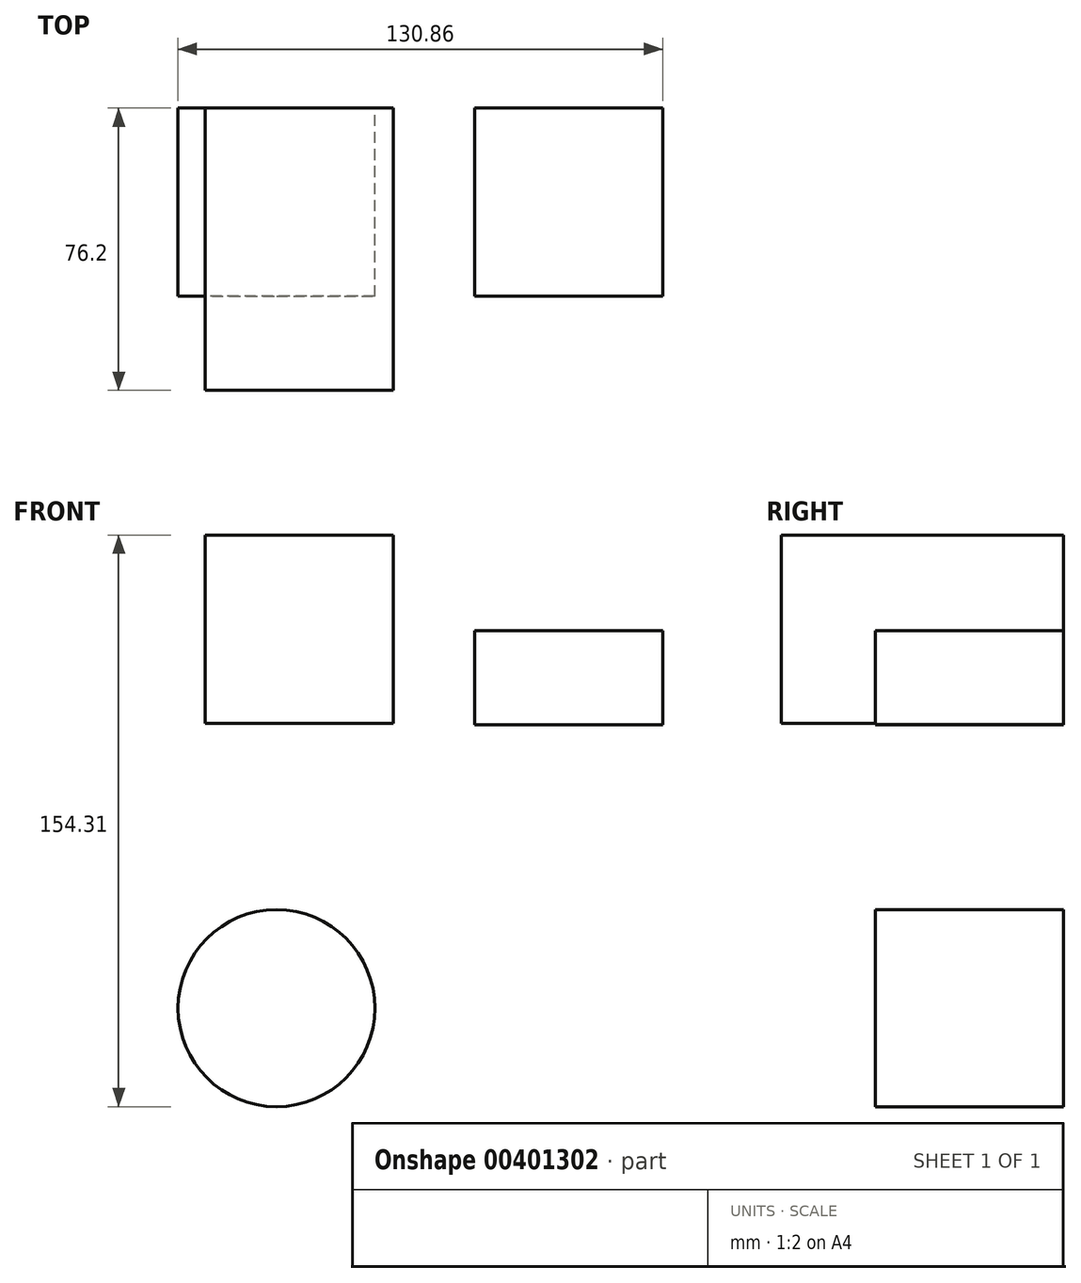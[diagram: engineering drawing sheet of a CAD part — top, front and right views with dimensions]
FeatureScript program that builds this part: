
annotation { "Feature Type Name" : "Feature", "Feature Type Description" : "" }
export const myFeature = defineFeature(function(context is Context, id is Id, definition is map)
    precondition{}
    {
        {
            var Q0;
            Q0=qCreatedBy(makeId("Front.planeOp"),FACE);
            var sketch = newSketch(context, id + "F0", { "sketchPlane" : qUnion([Q0])});
            skLineSegment(sketch, "E0.bottom", {"start": v(-61.9, 87.41) * mm, "end": v(-11.1, 87.41) * mm});
            skLineSegment(sketch, "E0.top", {"start": v(-61.9, 36.61) * mm, "end": v(-11.1, 36.61) * mm});
            skLineSegment(sketch, "E0.left", {"start": v(-61.9, 87.41) * mm, "end": v(-61.9, 36.61) * mm});
            skLineSegment(sketch, "E0.right", {"start": v(-11.1, 87.41) * mm, "end": v(-11.1, 36.61) * mm});
            skSolve(sketch);
        }
        {
            var Q0;
            Q0=qCreatedBy(makeId("Front.planeOp"),FACE);
            var sketch = newSketch(context, id + "F1", { "sketchPlane" : qUnion([Q0])});
            skLineSegment(sketch, "E1.bottom", {"start": v(10.86, 61.52) * mm, "end": v(61.66, 61.52) * mm});
            skLineSegment(sketch, "E1.top", {"start": v(10.86, 36.12) * mm, "end": v(61.66, 36.12) * mm});
            skLineSegment(sketch, "E1.left", {"start": v(10.86, 61.52) * mm, "end": v(10.86, 36.12) * mm});
            skLineSegment(sketch, "E1.right", {"start": v(61.66, 61.52) * mm, "end": v(61.66, 36.12) * mm});
            skSolve(sketch);
        }
        {
            var Q0;
            Q0=qCreatedBy(makeId("Front.planeOp"),FACE);
            var sketch = newSketch(context, id + "F2", { "sketchPlane" : qUnion([Q0])});
            skCircle(sketch, "E2", {"center": v(-42.62, -40.32) * mm, "radius": 26.58 * mm});
            skSolve(sketch);
        }
        {
            var Q0;
            Q0=makeQuery(id+"F0.imprint","IMPRINT",FACE,{"disambiguationData":[TD([[makeQuery(id+"F0.imprint","IMPRINT",EDGE,{"derivedFrom":sQuery(id+"F0.wireOp",EDGE,"E0.bottom")}),-1.0]])]});
            extrude(context, id + "F3", {"entities" : qUnion([Q0]), "depth" : 25.4 * mm});
        }
        {
            var Q0;
            Q0=makeQuery(id+"F1.imprint","IMPRINT",FACE,{"disambiguationData":[TD([[makeQuery(id+"F1.imprint","IMPRINT",EDGE,{"derivedFrom":sQuery(id+"F1.wireOp",EDGE,"E1.bottom")}),-1.0]])]});
            extrude(context, id + "F4", {"entities" : qUnion([Q0]), "depth" : 50.8 * mm});
        }
        {
            var Q0;
            Q0=makeQuery(id+"F2.imprint","IMPRINT",FACE,{"disambiguationData":[TD([[makeQuery(id+"F2.imprint","IMPRINT",EDGE,{"derivedFrom":sQuery(id+"F2.wireOp",EDGE,"E2")}),1.0]])]});
            extrude(context, id + "F5", {"entities" : qUnion([Q0]), "depth" : 50.8 * mm});
        }
        {
            var Q0;
            Q0=makeQuery(id+"F3.opExtrude","CAP_FACE",FACE,{"disambiguationData":[OSD([sQuery(id+"F0.wireOp",EDGE,"E0.bottom"),sQuery(id+"F0.wireOp",EDGE,"E0.top"),sQuery(id+"F0.wireOp",EDGE,"E0.left"),sQuery(id+"F0.wireOp",EDGE,"E0.right")])],"isStart":false});
            extrude(context, id + "F6", {"entities" : qUnion([Q0]), "operationType" : NewBodyOperationType.ADD, "depth" : 50.8 * mm});
        }
    });
